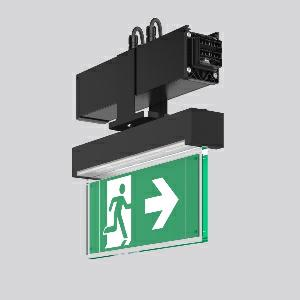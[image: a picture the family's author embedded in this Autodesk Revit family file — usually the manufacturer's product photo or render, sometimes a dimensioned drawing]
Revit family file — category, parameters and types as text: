
# Revit family: linedo_module_rz_9503rz_763_434_023_8ef5
name_source: partatom
category: Lighting Fixtures
units: mm (PartAtom-declared; Revit-internal decimal feet)

## family parameters
Cut with Voids When Loaded = No
Host = Face
Light Source = No
Part Type = Normal
Room Calculation Point = No
Round Connector Dimension = Use Diameter
Shared = No

## types (1)
- LINEDO Module RZ
    Apparent Load = 0 VA
    Default Elevation = 1800 mm
    Description = LINEDO, black, on/off
Continuous line luminaire, L 336 B 62 H 308, SBS, 3 h, MultiDigit
    Height = 308 mm
    Lamp = 0 x
    Length = 336 mm
    Luminous efficacy = 0 lm/W
    Manufacturer = RZB
    ModVariant = No
    Model = 9503RZ.763.434.023
    Mounting Place = Ceiling
    Mounting Type = Surface mounted
    Number of Poles = 1
    OnlyDefault = Yes
    Power Factor = 1
    Product Name = LINEDO Module RZ
    Product group = Surface mounted continuous line luminaire system
    ProductGroupID = 310
    Protection Class = Protection class I
    Protection Degree = IP 54
    RLX_Detail_Level = 1
    RLX_Emergency_Light_Flux = 0 lm
    RLX_Emergency_Type = 0
    RLX_Emergency_Type_DB = No
    RlxData = <blob elided: 37413 chars, md5=ac9d27a6>
    Standby Power = 0 W
    System Light Flux = 0 lm
    System Power = 0 W
    Type Comments = Product without accessories
    Type Image = 9503rz.763.434.023.jpg
    URL = http://relux.com
    VarID = ---
    Voltage = 0 V
    Weight = 0.00 kg
    Width = 62 mm  [stored 0.203412 ft]

note: [stored X ft] marks values corroborated as IEEE doubles in the binary element streams (Revit-internal decimal feet)

## geometry (parser evidence)
native form markers: Blend x4, Sweep x12
no freeform markers — native parametric forms only
